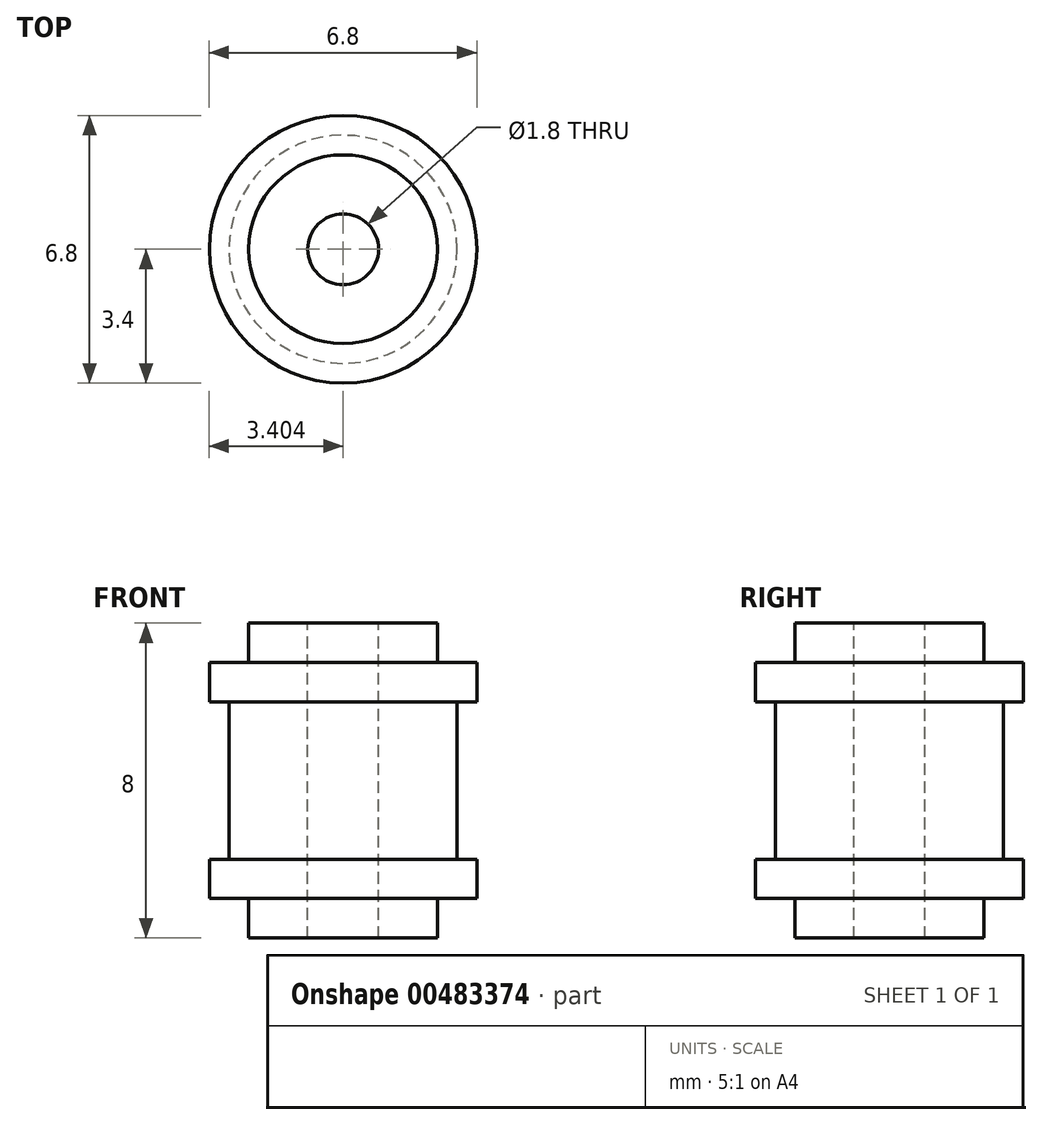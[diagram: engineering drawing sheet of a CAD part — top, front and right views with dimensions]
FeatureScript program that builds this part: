
annotation { "Feature Type Name" : "Feature", "Feature Type Description" : "" }
export const myFeature = defineFeature(function(context is Context, id is Id, definition is map)
    precondition{}
    {
        {
            var Q0;
            Q0=qCreatedBy(makeId("Front.planeOp"),FACE);
            var sketch = newSketch(context, id + "F0", { "sketchPlane" : qUnion([Q0])});
            skLineSegment(sketch, "E0", {"start": v(0, 5.64) * mm, "end": v(0, -5.64) * mm});
            skLineSegment(sketch, "E1", {"start": v(-1.72, 4.18) * mm, "end": v(-1.72, 3.18) * mm});
            skLineSegment(sketch, "E2", {"start": v(-1.72, 3.18) * mm, "end": v(-2.72, 3.18) * mm});
            skLineSegment(sketch, "E3", {"start": v(-2.72, 3.18) * mm, "end": v(-2.72, 2.18) * mm});
            skLineSegment(sketch, "E4", {"start": v(-2.72, 2.18) * mm, "end": v(-2.22, 2.18) * mm});
            skLineSegment(sketch, "E5", {"start": v(-2.22, 2.18) * mm, "end": v(-2.22, -1.82) * mm});
            skLineSegment(sketch, "E6", {"start": v(-2.22, -1.82) * mm, "end": v(-2.72, -1.82) * mm});
            skLineSegment(sketch, "E7", {"start": v(-2.72, -1.82) * mm, "end": v(-2.72, -2.82) * mm});
            skLineSegment(sketch, "E8", {"start": v(-2.72, -2.82) * mm, "end": v(-1.72, -2.82) * mm});
            skLineSegment(sketch, "E9", {"start": v(-1.72, -2.82) * mm, "end": v(-1.72, -3.82) * mm});
            skLineSegment(sketch, "E10", {"start": v(-1.72, -3.82) * mm, "end": v(-0.22, -3.82) * mm});
            skLineSegment(sketch, "E11", {"start": v(-1.72, 4.18) * mm, "end": v(-0.22, 4.18) * mm});
            skLineSegment(sketch, "E12", {"start": v(0.68, 5.97) * mm, "end": v(0.68, -7.64) * mm});
            skLineSegment(sketch, "E13", {"start": v(-0.22, 4.18) * mm, "end": v(-0.22, -3.82) * mm});
            skSolve(sketch);
        }
        {
            var Q0;
            Q0=makeQuery(id+"F0.imprint","IMPRINT",FACE,{"disambiguationData":[TD([[makeQuery(id+"F0.imprint","IMPRINT",EDGE,{"derivedFrom":sQuery(id+"F0.wireOp",EDGE,"E1")}),1.0]])]});
            var Q1;
            Q1=sQuery(id+"F0.wireOp",EDGE,"E12");
            revolve(context, id + "F1", {"entities" : qUnion([Q0]), "axis" : qUnion([Q1]), "revolveType" : RevolveType.FULL});
        }
    });
